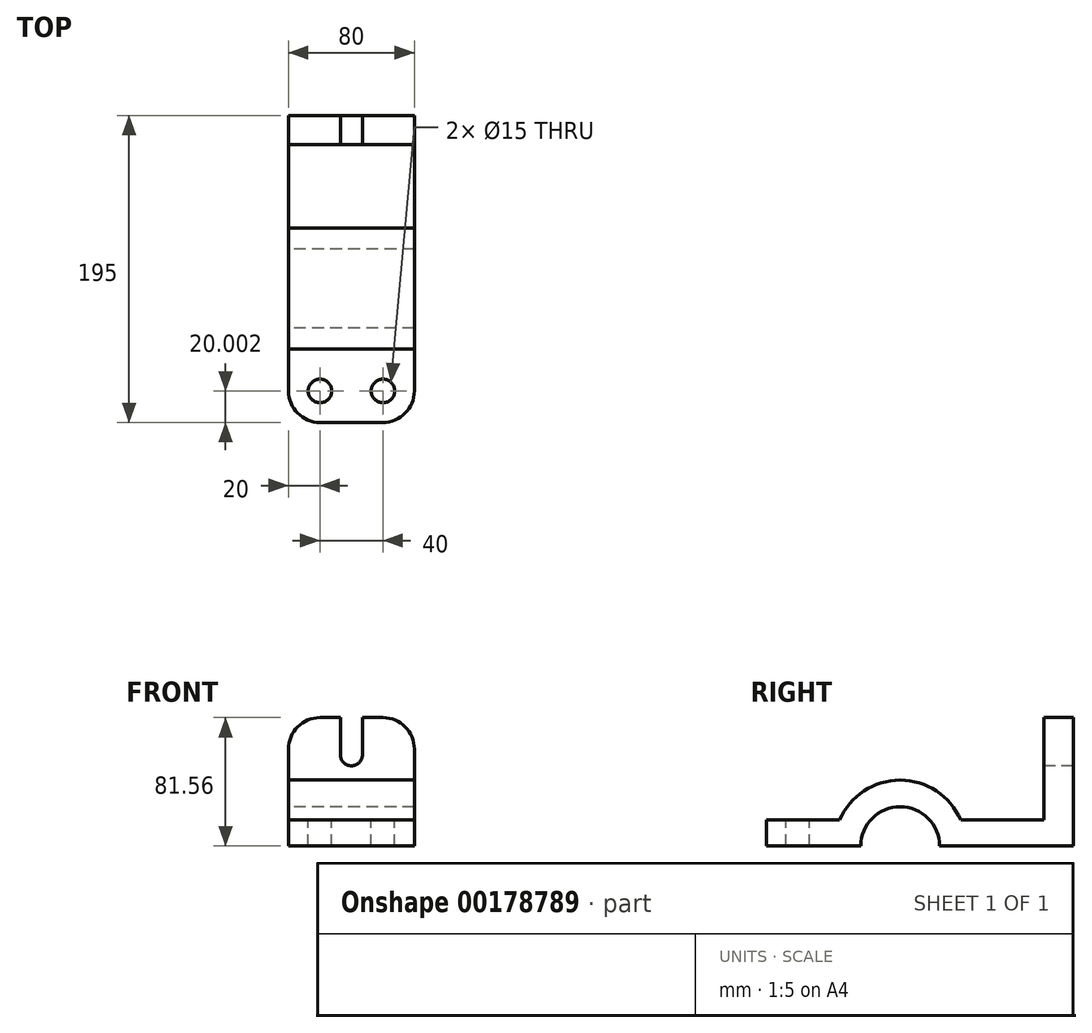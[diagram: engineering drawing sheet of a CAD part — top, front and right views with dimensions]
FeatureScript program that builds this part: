
annotation { "Feature Type Name" : "Feature", "Feature Type Description" : "" }
export const myFeature = defineFeature(function(context is Context, id is Id, definition is map)
    precondition{}
    {
        {
            var Q0;
            Q0=qCreatedBy(makeId("Right.planeOp"),FACE);
            var sketch = newSketch(context, id + "F0", { "sketchPlane" : qUnion([Q0])});
            skLineSegment(sketch, "E0", {"start": v(-110.24, -21.34) * mm, "end": v(-110.24, -37.96) * mm});
            skLineSegment(sketch, "E1", {"start": v(-110.24, -37.96) * mm, "end": v(-50.24, -37.96) * mm});
            skArc(sketch, "E2", {"start": v(-50.24, -37.96) * mm, "mid": v(-25.24, -12.96) * mm, "end": v(-0.24, -37.96) * mm});
            skLineSegment(sketch, "E3", {"start": v(-0.24, -37.96) * mm, "end": v(84.76, -37.96) * mm});
            skLineSegment(sketch, "E4", {"start": v(84.76, -37.96) * mm, "end": v(84.76, 43.6) * mm});
            skArc(sketch, "E5", {"start": v(-63.68, -21.34) * mm, "mid": v(-25.24, 3.92) * mm, "end": v(13.2, -21.34) * mm});
            skLineSegment(sketch, "E6", {"start": v(13.2, -21.34) * mm, "end": v(66.2, -21.34) * mm});
            skLineSegment(sketch, "E7", {"start": v(66.2, -21.34) * mm, "end": v(66.2, 43.6) * mm});
            skLineSegment(sketch, "E8", {"start": v(66.2, 43.6) * mm, "end": v(84.76, 43.6) * mm});
            skLineSegment(sketch, "E9", {"start": v(-110.24, -21.34) * mm, "end": v(-63.68, -21.34) * mm});
            skSolve(sketch);
        }
        {
            var Q0;
            Q0 = qSketchRegion(id + "F0", true);
            extrude(context, id + "F1", {"entities" : qUnion([Q0]), "endBound" : BoundingType.SYMMETRIC, "depth" : 80 * mm});
        }
        {
            var Q0;
            Q0=makeQuery(id+"F1.opExtrude","CAP_EDGE",EDGE,{"disambiguationData":[OSD([sQuery(id+"F0.wireOp",EDGE,"E0")])],"isStart":false});
            var Q1;
            Q1=makeQuery(id+"F1.opExtrude","CAP_EDGE",EDGE,{"disambiguationData":[OSD([sQuery(id+"F0.wireOp",EDGE,"E0")])],"isStart":true});
            var Q2;
            Q2=makeQuery(id+"F1.opExtrude","CAP_EDGE",EDGE,{"disambiguationData":[OSD([sQuery(id+"F0.wireOp",EDGE,"E8")])],"isStart":false});
            var Q3;
            Q3=makeQuery(id+"F1.opExtrude","CAP_EDGE",EDGE,{"disambiguationData":[OSD([sQuery(id+"F0.wireOp",EDGE,"E8")])],"isStart":true});
            fillet(context, id + "F2", {"entities" : qUnion([Q0, Q1, Q2, Q3]), "radius" : 20 * mm, "tangentPropagation" : true, "allowEdgeOverflow" : false});
        }
        {
            var Q0;
            Q0=makeQuery(id+"F1.opExtrude","SWEPT_FACE",FACE,{"disambiguationData":[OSD([sQuery(id+"F0.wireOp",EDGE,"E7")])]});
            var sketch = newSketch(context, id + "F3", { "sketchPlane" : qUnion([Q0])});
            skArc(sketch, "E10", {"start": v(-7, 20) * mm, "mid": v(0, 13) * mm, "end": v(7, 20) * mm});
            skLineSegment(sketch, "E11", {"start": v(7, 20) * mm, "end": v(7, 43.6) * mm});
            skLineSegment(sketch, "E12", {"start": v(7, 43.6) * mm, "end": v(-7, 43.6) * mm});
            skLineSegment(sketch, "E13", {"start": v(-7, 43.6) * mm, "end": v(-7, 20) * mm});
            skSolve(sketch);
        }
        {
            var Q0;
            Q0 = qSketchRegion(id + "F3", true);
            extrude(context, id + "F4", {"entities" : qUnion([Q0]), "operationType" : NewBodyOperationType.REMOVE, "endBound" : BoundingType.THROUGH_ALL, "oppositeDirection" : true, "depth" : 25 * mm});
        }
        {
            var Q0;
            Q0=makeQuery(id+"F1.opExtrude","SWEPT_FACE",FACE,{"disambiguationData":[OSD([sQuery(id+"F0.wireOp",EDGE,"E9")])]});
            var sketch = newSketch(context, id + "F5", { "sketchPlane" : qUnion([Q0])});
            skCircle(sketch, "E14", {"center": v(-20, -90.24) * mm, "radius": 7.5 * mm});
            skCircle(sketch, "E15", {"center": v(20, -90.24) * mm, "radius": 7.5 * mm});
            skSolve(sketch);
        }
        {
            var Q0;
            Q0 = qSketchRegion(id + "F5", true);
            extrude(context, id + "F6", {"entities" : qUnion([Q0]), "operationType" : NewBodyOperationType.REMOVE, "endBound" : BoundingType.THROUGH_ALL, "oppositeDirection" : true, "depth" : 25 * mm});
        }
    });
